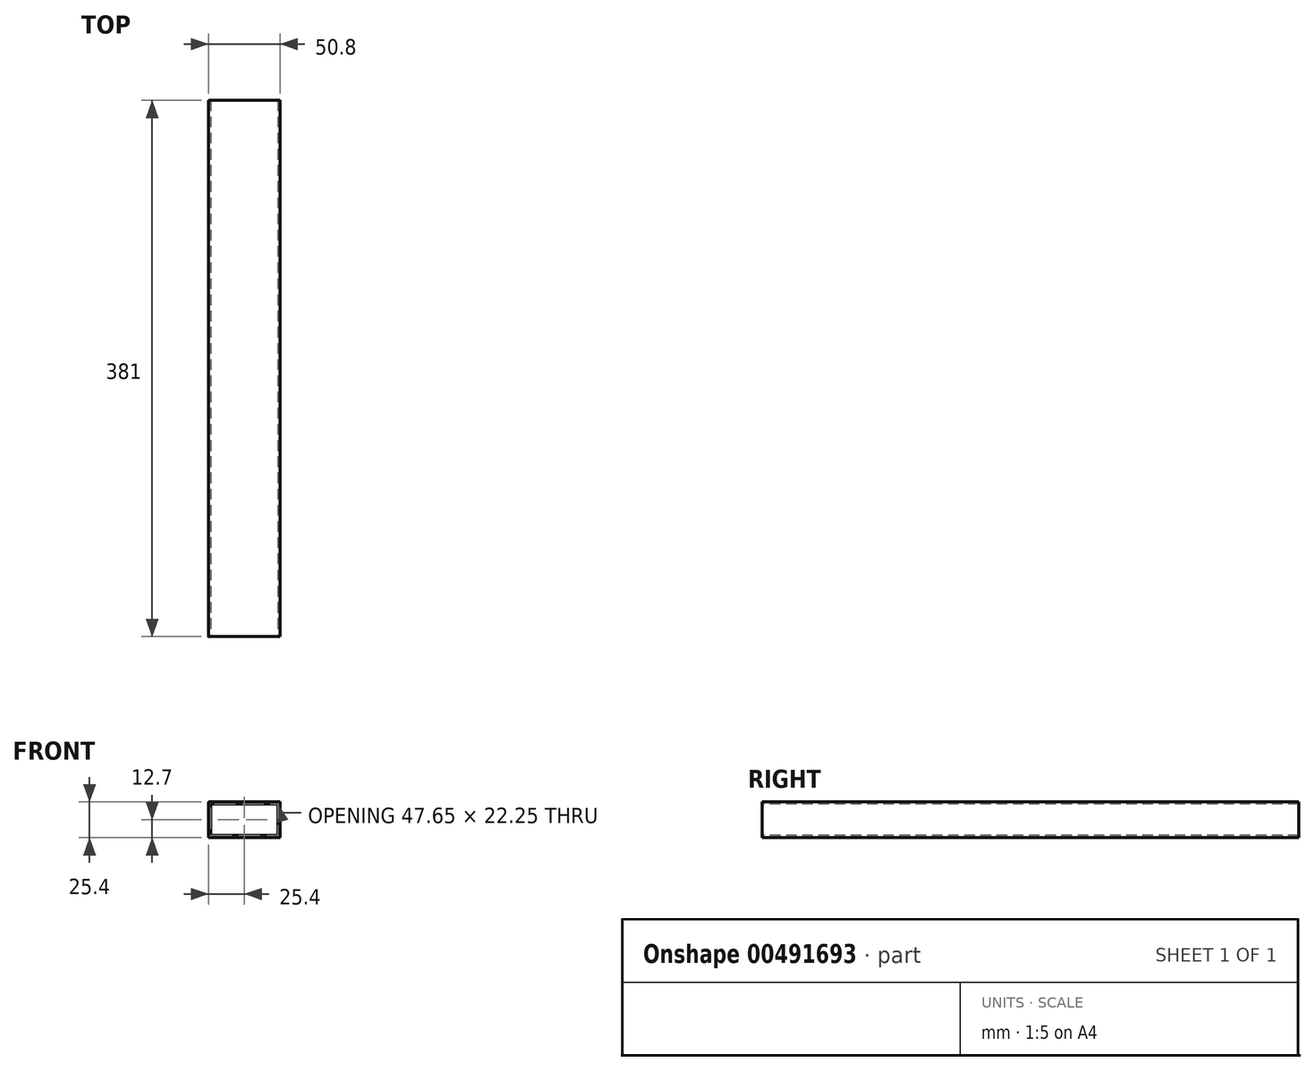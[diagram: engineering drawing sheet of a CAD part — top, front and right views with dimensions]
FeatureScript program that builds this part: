
annotation { "Feature Type Name" : "Feature", "Feature Type Description" : "" }
export const myFeature = defineFeature(function(context is Context, id is Id, definition is map)
    precondition{}
    {
        {
            var Q0;
            Q0=qCreatedBy(makeId("Front.planeOp"),FACE);
            var sketch = newSketch(context, id + "F0", { "sketchPlane" : qUnion([Q0])});
            skLineSegment(sketch, "E0.bottom", {"start": v(25.4, 12.7) * mm, "end": v(-25.4, 12.7) * mm});
            skLineSegment(sketch, "E0.top", {"start": v(25.4, -12.7) * mm, "end": v(-25.4, -12.7) * mm});
            skLineSegment(sketch, "E0.left", {"start": v(25.4, 12.7) * mm, "end": v(25.4, -12.7) * mm});
            skLineSegment(sketch, "E0.right", {"start": v(-25.4, 12.7) * mm, "end": v(-25.4, -12.7) * mm});
            skPoint(sketch, "E0.middle", {"position": v(0, 0) * mm});
            skSolve(sketch);
        }
        {
            var Q0;
            Q0=qSketchRegion(id+"F0",true);
            extrude(context, id + "F1", {"entities" : qUnion([Q0]), "depth" : 381 * mm, "offsetDistance" : 25.4 * mm});
        }
        {
            var Q0;
            Q0=makeQuery(id+"F1.opExtrude","CAP_FACE",FACE,{"disambiguationData":[OSD([sQuery(id+"F0.wireOp",EDGE,"E0.bottom"),sQuery(id+"F0.wireOp",EDGE,"E0.top"),sQuery(id+"F0.wireOp",EDGE,"E0.left"),sQuery(id+"F0.wireOp",EDGE,"E0.right")])],"isStart":false});
            var sketch = newSketch(context, id + "F2", { "sketchPlane" : qUnion([Q0])});
            skLineSegment(sketch, "E1.bottom", {"start": v(23.83, 11.13) * mm, "end": v(-23.83, 11.13) * mm});
            skLineSegment(sketch, "E1.top", {"start": v(23.83, -11.13) * mm, "end": v(-23.83, -11.13) * mm});
            skLineSegment(sketch, "E1.left", {"start": v(23.83, 11.13) * mm, "end": v(23.83, -11.13) * mm});
            skLineSegment(sketch, "E1.right", {"start": v(-23.83, 11.13) * mm, "end": v(-23.83, -11.13) * mm});
            skPoint(sketch, "E1.middle", {"position": v(0, 0) * mm});
            skSolve(sketch);
        }
        {
            var Q0;
            Q0=qSketchRegion(id+"F2",true);
            extrude(context, id + "F3", {"entities" : qUnion([Q0]), "operationType" : NewBodyOperationType.REMOVE, "endBound" : BoundingType.UP_TO_NEXT, "oppositeDirection" : true, "depth" : 25.4 * mm});
        }
        {
            var Q0;
            Q0=makeQuery(id+"F3.boolean.opBoolean","COPY",EDGE,{"derivedFrom":makeQuery(id+"F3.opExtrude","SWEPT_EDGE",EDGE,{"disambiguationData":[OSD([sQuery(id+"F2.wireOp",EDGE,"E1.top"),sQuery(id+"F2.wireOp",EDGE,"E1.left")])]})});
            var Q1;
            Q1=makeQuery(id+"F3.boolean.opBoolean","COPY",EDGE,{"derivedFrom":makeQuery(id+"F3.opExtrude","SWEPT_EDGE",EDGE,{"disambiguationData":[OSD([sQuery(id+"F2.wireOp",EDGE,"E1.bottom"),sQuery(id+"F2.wireOp",EDGE,"E1.left")])]})});
            var Q2;
            Q2=makeQuery(id+"F3.boolean.opBoolean","COPY",EDGE,{"derivedFrom":makeQuery(id+"F3.opExtrude","SWEPT_EDGE",EDGE,{"disambiguationData":[OSD([sQuery(id+"F2.wireOp",EDGE,"E1.top"),sQuery(id+"F2.wireOp",EDGE,"E1.right")])]})});
            var Q3;
            Q3=makeQuery(id+"F3.boolean.opBoolean","COPY",EDGE,{"derivedFrom":makeQuery(id+"F3.opExtrude","SWEPT_EDGE",EDGE,{"disambiguationData":[OSD([sQuery(id+"F2.wireOp",EDGE,"E1.bottom"),sQuery(id+"F2.wireOp",EDGE,"E1.right")])]})});
            fillet(context, id + "F4", {"entities" : qUnion([Q0, Q1, Q2, Q3]), "radius" : 1.52 * mm, "tangentPropagation" : true, "allowEdgeOverflow" : false});
        }
        {
            var Q0;
            Q0=makeQuery(id+"F1.opExtrude","SWEPT_EDGE",EDGE,{"disambiguationData":[OSD([sQuery(id+"F0.wireOp",EDGE,"E0.bottom"),sQuery(id+"F0.wireOp",EDGE,"E0.right")])]});
            var Q1;
            Q1=makeQuery(id+"F1.opExtrude","SWEPT_EDGE",EDGE,{"disambiguationData":[OSD([sQuery(id+"F0.wireOp",EDGE,"E0.bottom"),sQuery(id+"F0.wireOp",EDGE,"E0.left")])]});
            var Q2;
            Q2=makeQuery(id+"F1.opExtrude","SWEPT_EDGE",EDGE,{"disambiguationData":[OSD([sQuery(id+"F0.wireOp",EDGE,"E0.top"),sQuery(id+"F0.wireOp",EDGE,"E0.left")])]});
            var Q3;
            Q3=makeQuery(id+"F1.opExtrude","SWEPT_EDGE",EDGE,{"disambiguationData":[OSD([sQuery(id+"F0.wireOp",EDGE,"E0.top"),sQuery(id+"F0.wireOp",EDGE,"E0.right")])]});
            fillet(context, id + "F5", {"entities" : qUnion([Q0, Q1, Q2, Q3]), "radius" : 0.25 * mm, "tangentPropagation" : true, "allowEdgeOverflow" : false});
        }
    });
